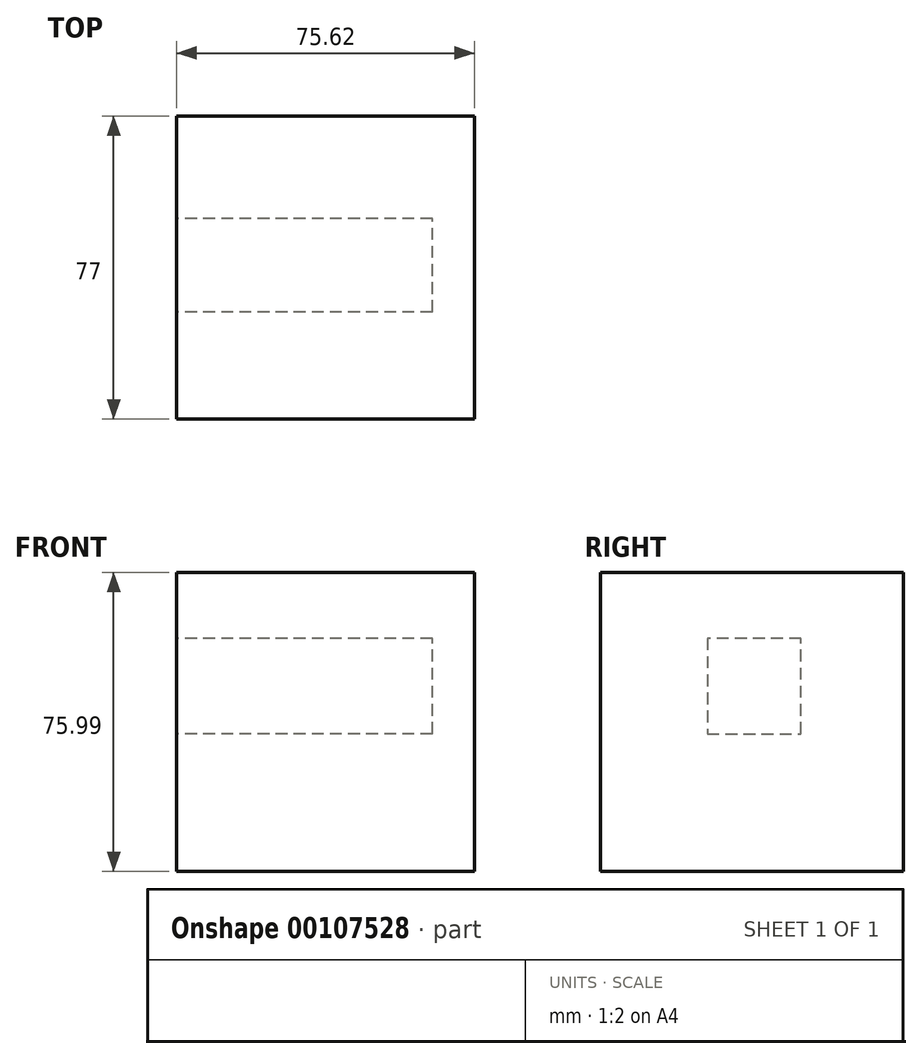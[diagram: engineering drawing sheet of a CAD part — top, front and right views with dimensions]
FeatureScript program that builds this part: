
annotation { "Feature Type Name" : "Feature", "Feature Type Description" : "" }
export const myFeature = defineFeature(function(context is Context, id is Id, definition is map)
    precondition{}
    {
        {
            var Q0;
            Q0=qCreatedBy(makeId("Front.planeOp"),FACE);
            var sketch = newSketch(context, id + "F0", { "sketchPlane" : qUnion([Q0])});
            skLineSegment(sketch, "E0", {"start": v(0, 0) * mm, "end": v(0, 75.99) * mm});
            skLineSegment(sketch, "E1", {"start": v(0, 75.99) * mm, "end": v(75.62, 75.99) * mm});
            skLineSegment(sketch, "E2", {"start": v(75.62, 75.99) * mm, "end": v(75.62, 0) * mm});
            skLineSegment(sketch, "E3", {"start": v(75.62, 0) * mm, "end": v(0, 0) * mm});
            skSolve(sketch);
        }
        {
            var Q0;
            Q0=makeQuery(id+"F0.imprint","IMPRINT",FACE,{"disambiguationData":[TD([[makeQuery(id+"F0.imprint","IMPRINT",EDGE,{"derivedFrom":sQuery(id+"F0.wireOp",EDGE,"E0")}),-1.0]])]});
            extrude(context, id + "F1", {"entities" : qUnion([Q0]), "depth" : 77 * mm});
        }
        {
            var Q0;
            Q0=qCreatedBy(makeId("Right.planeOp"),FACE);
            var sketch = newSketch(context, id + "F2", { "sketchPlane" : qUnion([Q0])});
            skLineSegment(sketch, "E4", {"start": v(0, 0) * mm, "end": v(-26.02, 28.6) * mm});
            skLineSegment(sketch, "E5", {"start": v(-26.02, 28.6) * mm, "end": v(-26.02, 59.3) * mm});
            skLineSegment(sketch, "E6", {"start": v(-26.02, 59.3) * mm, "end": v(-49.84, 59.3) * mm});
            skLineSegment(sketch, "E7", {"start": v(-49.84, 59.3) * mm, "end": v(-49.84, 34.99) * mm});
            skLineSegment(sketch, "E8", {"start": v(-49.84, 34.99) * mm, "end": v(-26.02, 34.99) * mm});
            skSolve(sketch);
        }
        {
            var Q0;
            {var subQ0=sQuery(id+"F2.wireOp",EDGE,"E6");Q0=makeQuery(id+"F2.imprint","IMPRINT",FACE,{"disambiguationData":[TD([[makeQuery(id+"F2.imprint","IMPRINT",EDGE,{"derivedFrom":subQ0}),1.0]])]});}
            extrude(context, id + "F3", {"entities" : qUnion([Q0]), "operationType" : NewBodyOperationType.REMOVE, "depth" : 64.92 * mm});
        }
    });
